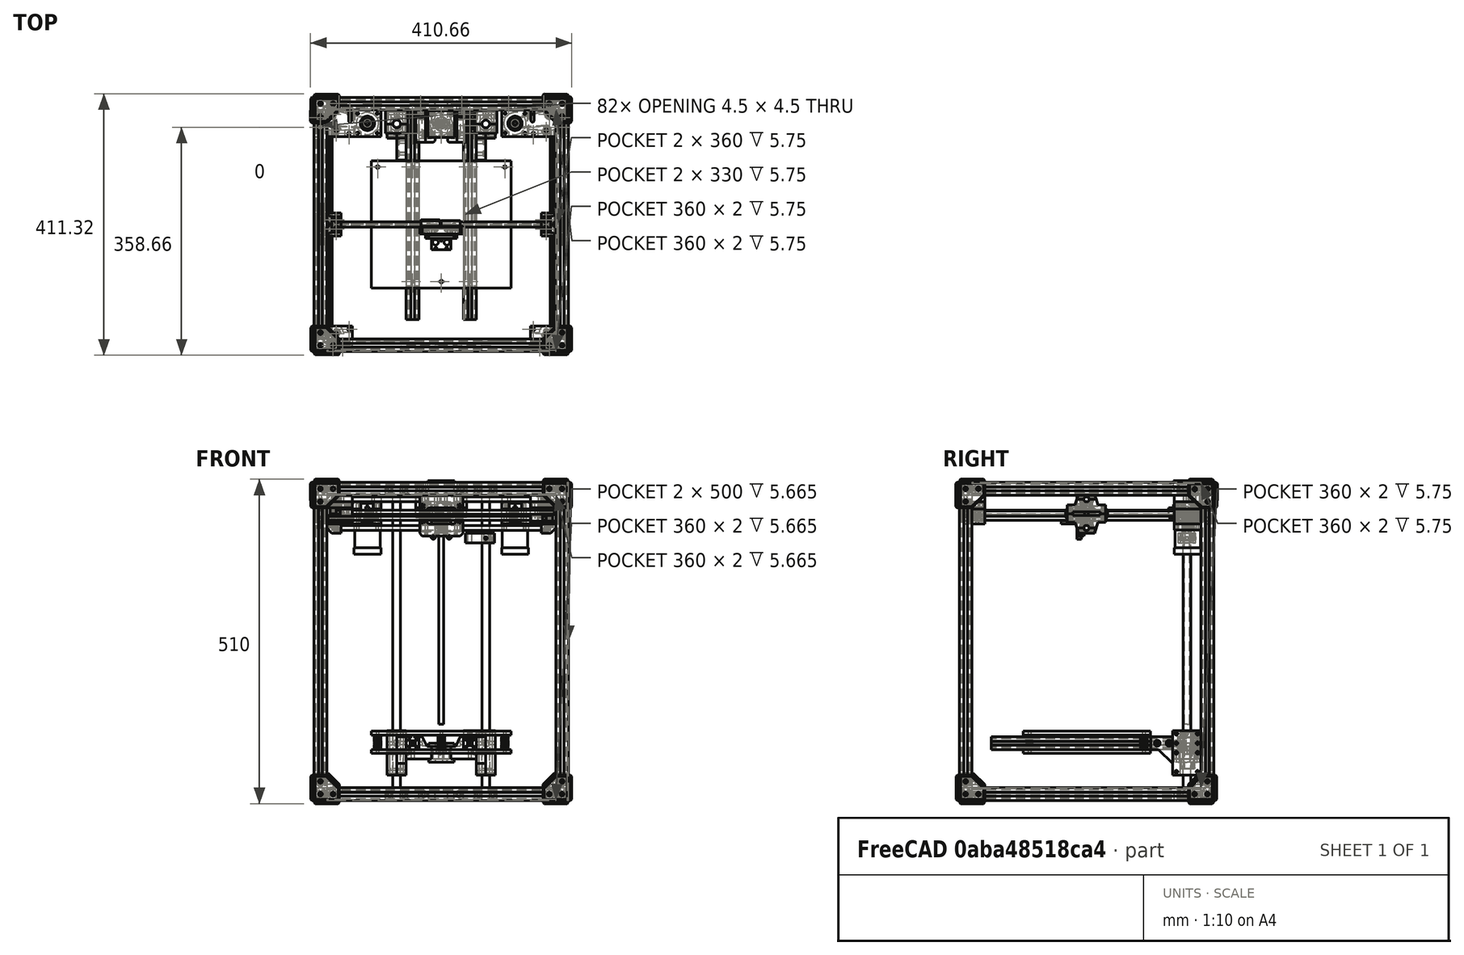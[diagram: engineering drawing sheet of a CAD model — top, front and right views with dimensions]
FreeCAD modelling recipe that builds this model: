
FCSTD DOCUMENT  (FreeCAD 0.16R5937 (Git))
Label: RepRap-XY-Iteration-2-Assembly
License: CC-BY 3.0
LicenseURL: http://creativecommons.org/licenses/by/3.0/
objects: Part::Feature×185, Part::Prism×30, Part::Fuse×25, Part::Box×15, Part::FeaturePython×6, Part::Cylinder×6, Part::Cut×6, Part::Extrusion×3, Part::MultiFuse×3, Part::Mirroring×1
note: 280 computed .brp shape members not serialized (recipe doc carries the construction recipe); baked Part::Feature solids carry a one-line shape summary decoded from their .brp

FEATURE [Part::Feature] Part__Feature  label="Nema-17"
  shape: bbox 42 x 42 x 74.5 mm, 37 faces (baked)
FEATURE [Part::Feature] Part__Feature001  label="Nema-018"
  shape: bbox 42 x 42 x 74.5 mm, 37 faces (baked)
FEATURE [Part::Feature] Part__Feature002  label="Nema-019"
  Placement = pos=(0,0,10) rot=(0,0,1;0rad)
  shape: bbox 42 x 42 x 74.5 mm, 37 faces (baked)
FEATURE [Part::Feature] Part__Feature004  label="F624zz-bearing"
  shape: bbox 15 x 15 x 5 mm, 15 faces (baked)
FEATURE [Part::Feature] Part__Feature005  label="624-bearing"
  shape: bbox 13 x 13 x 5 mm, 10 faces (baked)
FEATURE [Part::Feature] Part__Feature006  label="spacer-1"
  shape: bbox 10 x 10 x 9.4 mm, 6 faces (baked)
FEATURE [Part::Feature] Part__Feature007  label="F624zz-bearing001"
  shape: bbox 15 x 15 x 5 mm, 15 faces (baked)
FEATURE [Part::Feature] Part__Feature008  label="624-bearing001"
  shape: bbox 13 x 13 x 5 mm, 10 faces (baked)
FEATURE [Part::Feature] Part__Feature009  label="washer-M4"
  shape: bbox 8 x 8 x 0.8 mm, 6 faces (baked)
FEATURE [Part::Feature] Part__Feature010  label="washer-M005"
  shape: bbox 8 x 8 x 0.8 mm, 6 faces (baked)
FEATURE [Part::Feature] Part__Feature011  label="F624zz-bearing002"
  shape: bbox 15 x 15 x 5 mm, 15 faces (baked)
FEATURE [Part::Feature] Part__Feature012  label="624-bearing002"
  shape: bbox 13 x 13 x 5 mm, 10 faces (baked)
FEATURE [Part::Feature] Part__Feature013  label="washer-M006"
  shape: bbox 8 x 8 x 0.8 mm, 6 faces (baked)
FEATURE [Part::Feature] Part__Feature014  label="washer-M007"
  shape: bbox 8 x 8 x 0.8 mm, 6 faces (baked)
FEATURE [Part::Feature] Part__Feature015  label="F624zz-bearing003"
  shape: bbox 15 x 15 x 5 mm, 15 faces (baked)
FEATURE [Part::Feature] Part__Feature016  label="624-bearing003"
  shape: bbox 13 x 13 x 5 mm, 10 faces (baked)
FEATURE [Part::Feature] Part__Feature017  label="washer-M008"
  shape: bbox 8 x 8 x 0.8 mm, 6 faces (baked)
FEATURE [Part::Feature] Part__Feature018  label="washer-M009"
  shape: bbox 8 x 8 x 0.8 mm, 6 faces (baked)
FEATURE [Part::Feature] Part__Feature019  label="F624zz-bearing004"
  shape: bbox 15 x 15 x 5 mm, 15 faces (baked)
FEATURE [Part::Feature] Part__Feature020  label="624-bearing004"
  shape: bbox 13 x 13 x 5 mm, 10 faces (baked)
FEATURE [Part::Feature] Part__Feature021  label="washer-M010"
  shape: bbox 8 x 8 x 0.8 mm, 6 faces (baked)
FEATURE [Part::Feature] Part__Feature022  label="washer-M011"
  shape: bbox 8 x 8 x 0.8 mm, 6 faces (baked)
FEATURE [Part::Feature] Part__Feature023  label="washer-M012"
  shape: bbox 8 x 8 x 0.8 mm, 6 faces (baked)
FEATURE [Part::Feature] Part__Feature024  label="washer-M013"
  shape: bbox 8 x 8 x 0.8 mm, 6 faces (baked)
FEATURE [Part::Feature] Part__Feature025  label="F624zz-bearing005"
  shape: bbox 15 x 15 x 5 mm, 15 faces (baked)
FEATURE [Part::Feature] Part__Feature026  label="624-bearing005"
  shape: bbox 13 x 13 x 5 mm, 10 faces (baked)
FEATURE [Part::Feature] Part__Feature027  label="spacer-002"
  shape: bbox 10 x 10 x 9.4 mm, 6 faces (baked)
FEATURE [Part::Feature] Part__Feature028  label="washer-M014"
  shape: bbox 8 x 8 x 0.8 mm, 6 faces (baked)
FEATURE [Part::Feature] Part__Feature029  label="washer-M015"
  shape: bbox 8 x 8 x 0.8 mm, 6 faces (baked)
FEATURE [Part::Feature] Part__Feature030  label="F624zz-bearing006"
  shape: bbox 15 x 15 x 5 mm, 15 faces (baked)
FEATURE [Part::Feature] Part__Feature031  label="624-bearing006"
  shape: bbox 13 x 13 x 5 mm, 10 faces (baked)
FEATURE [Part::Feature] Part__Feature032  label="spacer-003"
  shape: bbox 10 x 10 x 9.4 mm, 6 faces (baked)
FEATURE [Part::Feature] Part__Feature033  label="washer-M016"
  shape: bbox 8 x 8 x 0.8 mm, 6 faces (baked)
FEATURE [Part::Feature] Part__Feature034  label="washer-M017"
  shape: bbox 8 x 8 x 0.8 mm, 6 faces (baked)
FEATURE [Part::Feature] Part__Feature035  label="F624zz-bearing007"
  shape: bbox 15 x 15 x 5 mm, 15 faces (baked)
FEATURE [Part::Feature] Part__Feature036  label="624-bearing007"
  shape: bbox 13 x 13 x 5 mm, 10 faces (baked)
FEATURE [Part::Feature] Part__Feature037  label="spacer-004"
  shape: bbox 10 x 10 x 9.4 mm, 6 faces (baked)
FEATURE [Part::Feature] Part__Feature038  label="washer-M018"
  shape: bbox 8 x 8 x 0.8 mm, 6 faces (baked)
FEATURE [Part::Feature] Part__Feature039  label="washer-M019"
  shape: bbox 8 x 8 x 0.8 mm, 6 faces (baked)
FEATURE [Part::Feature] Part__Feature040  label="F624zz-bearing008"
  shape: bbox 15 x 15 x 5 mm, 15 faces (baked)
FEATURE [Part::Feature] Part__Feature041  label="624-bearing008"
  shape: bbox 13 x 13 x 5 mm, 10 faces (baked)
FEATURE [Part::Feature] Part__Feature042  label="washer-M020"
  shape: bbox 8 x 8 x 0.8 mm, 6 faces (baked)
FEATURE [Part::Feature] Part__Feature043  label="washer-M021"
  shape: bbox 8 x 8 x 0.8 mm, 6 faces (baked)
FEATURE [Part::Feature] Part__Feature044  label="F624zz-bearing009"
  shape: bbox 15 x 15 x 5 mm, 15 faces (baked)
FEATURE [Part::Feature] Part__Feature045  label="624-bearing009"
  shape: bbox 13 x 13 x 5 mm, 10 faces (baked)
FEATURE [Part::Feature] Part__Feature046  label="washer-M022"
  shape: bbox 8 x 8 x 0.8 mm, 6 faces (baked)
FEATURE [Part::Feature] Part__Feature047  label="washer-M023"
  shape: bbox 8 x 8 x 0.8 mm, 6 faces (baked)
FEATURE [Part::Feature] Part__Feature048  label="F624zz-bearing010"
  shape: bbox 15 x 15 x 5 mm, 15 faces (baked)
FEATURE [Part::Feature] Part__Feature049  label="624-bearing010"
  shape: bbox 13 x 13 x 5 mm, 10 faces (baked)
FEATURE [Part::Feature] Part__Feature050  label="washer-M024"
  shape: bbox 8 x 8 x 0.8 mm, 6 faces (baked)
FEATURE [Part::Feature] Part__Feature051  label="washer-M025"
  shape: bbox 8 x 8 x 0.8 mm, 6 faces (baked)
FEATURE [Part::Feature] Part__Feature052  label="F624zz-bearing011"
  shape: bbox 15 x 15 x 5 mm, 15 faces (baked)
FEATURE [Part::Feature] Part__Feature053  label="624-bearing011"
  shape: bbox 13 x 13 x 5 mm, 10 faces (baked)
FEATURE [Part::Feature] Part__Feature054  label="washer-M026"
  shape: bbox 8 x 8 x 0.8 mm, 6 faces (baked)
FEATURE [Part::Feature] Part__Feature055  label="washer-M027"
  shape: bbox 8 x 8 x 0.8 mm, 6 faces (baked)
FEATURE [Part::Feature] Part__Feature057  label="Alu-20x20x360"
  Placement = pos=(0,0,-110) rot=(0,0,1;0rad)
  shape: bbox 360 x 20 x 20 mm, 40 faces (baked)
FEATURE [Part::Feature] Part__Feature058  label="Alu-20x20x361"
  Placement = pos=(0,0,-110) rot=(0,0,1;0rad)
  shape: bbox 20 x 360 x 20 mm, 40 faces (baked)
FEATURE [Part::Feature] Part__Feature059  label="Alu-20x20x362"
  Placement = pos=(0,0,-110) rot=(0,0,1;0rad)
  shape: bbox 20 x 360 x 20 mm, 40 faces (baked)
FEATURE [Part::Feature] Part__Feature060  label="Alu-20x20x363"
  Placement = pos=(0,0,-110) rot=(0,0,1;0rad)
  shape: bbox 360 x 20 x 20 mm, 40 faces (baked)
FEATURE [Part::Feature] Part__Feature064  label="Alu-20x20x367"
  Placement = pos=(0,0,10) rot=(0,0,1;0rad)
  shape: bbox 360 x 20 x 20 mm, 40 faces (baked)
FEATURE [Part::Feature] Part__Feature065  label="Alu-20x20x368"
  Placement = pos=(0,0,10) rot=(0,0,1;0rad)
  shape: bbox 20 x 360 x 20 mm, 40 faces (baked)
FEATURE [Part::Feature] Part__Feature066  label="Alu-20x20x369"
  Placement = pos=(0,0,10) rot=(0,0,1;0rad)
  shape: bbox 20 x 360 x 20 mm, 40 faces (baked)
FEATURE [Part::Feature] Part__Feature067  label="Alu-20x20x370"
  Placement = pos=(0,0,10) rot=(0,0,1;0rad)
  shape: bbox 360 x 20 x 20 mm, 40 faces (baked)
FEATURE [Part::Feature] Part__Feature068  label="smooth-bar-8x330"
  Placement = pos=(0,20,22.5) rot=(0,0,1;0rad)
  shape: bbox 330 x 8 x 8 mm, 4 faces (baked)
FEATURE [Part::Feature] Part__Feature069  label="smooth-bar-8x331"
  shape: bbox 8 x 330 x 8 mm, 4 faces (baked)
FEATURE [Part::Feature] Part__Feature070  label="smooth-bar-8x332"
  shape: bbox 8 x 330 x 8 mm, 4 faces (baked)
FEATURE [Part::Feature] Part__Feature071  label="smooth-bar-8x333"
  Placement = pos=(0,-20,-22.5) rot=(0,0,1;0rad)
  shape: bbox 330 x 8 x 8 mm, 4 faces (baked)
FEATURE [Part::Feature] Part__Feature072  label="Alu-20x20x330"
  Placement = pos=(0,0,-280) rot=(0,0,1;0rad)
  shape: bbox 20 x 330 x 20 mm, 40 faces (baked)
FEATURE [Part::Feature] Part__Feature073  label="Alu-20x20x371"
  Placement = pos=(0,0,-280) rot=(0,0,1;0rad)
  shape: bbox 20 x 330 x 20 mm, 41 faces (baked)
FEATURE [Part::Feature] Part__Feature077  label="GT2-belt"
  shape: bbox 351 x 379 x 6 mm, 36 faces (baked)
FEATURE [Part::Feature] Part__Feature078  label="GT2-belt001"
  shape: bbox 351 x 379 x 6 mm, 36 faces (baked)
FEATURE [Part::Feature] Part__Feature083  label="idler-block"
  shape: bbox 60 x 40 x 23 mm, 30 faces (baked)
FEATURE [Part::Feature] Part__Feature084  label="idler-block-top"
  shape: bbox 60 x 40 x 12 mm, 28 faces (baked)
FEATURE [Part::Feature] Part__Feature085  label="idler-block-mirrored"
  shape: bbox 60 x 40 x 23 mm, 30 faces (baked)
FEATURE [Part::Feature] Part__Feature086  label="idler-block-top-mirrored"
  shape: bbox 60 x 40 x 12 mm, 28 faces (baked)
FEATURE [Part::Feature] Part__Feature088  label="624-bearing012"
  shape: bbox 13 x 13 x 5 mm, 10 faces (baked)
FEATURE [Part::Feature] Part__Feature089  label="624-bearing013"
  shape: bbox 13 x 13 x 5 mm, 10 faces (baked)
FEATURE [Part::Feature] Part__Feature090  label="Z-axis-clamp-1"
  Placement = pos=(0,0,-110) rot=(0,0,1;0rad)
  shape: bbox 35 x 22 x 20 mm, 12 faces (baked)
FEATURE [Part::Feature] Part__Feature091  label="Z-axis-clamp-002"
  Placement = pos=(0,0,-110) rot=(0,0,1;0rad)
  shape: bbox 35 x 22 x 20 mm, 12 faces (baked)
FEATURE [Part::Feature] Part__Feature092  label="Z-axis-clamp-003"
  Placement = pos=(0,0,10) rot=(0,0,1;0rad)
  shape: bbox 35 x 22 x 20 mm, 12 faces (baked)
FEATURE [Part::Feature] Part__Feature093  label="Z-axis-clamp-004"
  Placement = pos=(0,0,10) rot=(0,0,1;0rad)
  shape: bbox 35 x 22 x 20 mm, 12 faces (baked)
FEATURE [Part::Feature] Part__Feature094  label="spacer-7mm"
  shape: bbox 10 x 10 x 7 mm, 6 faces (baked)
FEATURE [Part::Feature] Part__Feature095  label="spacer-7mm001"
  shape: bbox 10 x 10 x 7 mm, 6 faces (baked)
FEATURE [Part::Feature] Part__Feature096  label="spacer-9mm4"
  shape: bbox 10 x 10 x 9.4 mm, 6 faces (baked)
FEATURE [Part::Feature] Part__Feature097  label="spacer-9mm005"
  shape: bbox 10 x 10 x 9.4 mm, 6 faces (baked)
FEATURE [Part::Feature] Part__Feature098  label="spacer-9mm006"
  shape: bbox 10 x 10 x 9.4 mm, 6 faces (baked)
FEATURE [Part::Feature] Part__Feature099  label="spacer-9mm007"
  shape: bbox 10 x 10 x 9.4 mm, 6 faces (baked)
FEATURE [Part::Feature] Part__Feature100  label="spacer-9mm008"
  shape: bbox 10 x 10 x 9.4 mm, 6 faces (baked)
FEATURE [Part::Feature] Part__Feature101  label="spacer-9mm009"
  shape: bbox 10 x 10 x 9.4 mm, 6 faces (baked)
FEATURE [Part::Feature] Part__Feature102  label="spacer16mm4"
  shape: bbox 10 x 10 x 16.4 mm, 6 faces (baked)
FEATURE [Part::Feature] Part__Feature103  label="spacer16mm005"
  shape: bbox 10 x 10 x 16.4 mm, 6 faces (baked)
FEATURE [Part::Feature] Part__Feature104  label="spacer16mm006"
  shape: bbox 10 x 10 x 16.4 mm, 6 faces (baked)
FEATURE [Part::Feature] Part__Feature105  label="washer-M028"
  shape: bbox 8 x 8 x 0.8 mm, 6 faces (baked)
FEATURE [Part::Feature] Part__Feature106  label="Z-axis-clamp-2"
  Placement = pos=(0,0,10) rot=(0,0,1;0rad)
  shape: bbox 35 x 15 x 20 mm, 18 faces (baked)
FEATURE [Part::Feature] Part__Feature107  label="Z-axis-clamp-005"
  Placement = pos=(0,0,10) rot=(0,0,1;0rad)
  shape: bbox 35 x 15 x 20 mm, 18 faces (baked)
FEATURE [Part::Feature] Part__Feature108  label="Z-axis-clamp-006"
  Placement = pos=(0,0,-110) rot=(0,0,1;0rad)
  shape: bbox 35 x 15 x 20 mm, 18 faces (baked)
FEATURE [Part::Feature] Part__Feature109  label="Z-axis-clamp-007"
  Placement = pos=(0,0,-110) rot=(0,0,1;0rad)
  shape: bbox 35 x 15 x 20 mm, 18 faces (baked)
FEATURE [Part::Feature] Part__Feature122  label="pulley"
  shape: bbox 17.78 x 17.78 x 16.13 mm, 138 faces (baked)
FEATURE [Part::Feature] Part__Feature123  label="pulley001"
  shape: bbox 17.78 x 17.78 x 16.13 mm, 138 faces (baked)
FEATURE [Part::Feature] Part__Feature130  label="Z-motor-mount"
  Placement = pos=(0,0,10) rot=(0,0,1;0rad)
  shape: bbox 30.05 x 100 x 85.05 mm, 39 faces (baked)
FEATURE [Part::Feature] Part__Feature131  label="Z-motor-mount-mirrored"
  Placement = pos=(0,0,10) rot=(0,0,1;0rad)
  shape: bbox 30.05 x 100 x 85.05 mm, 39 faces (baked)
FEATURE [Part::Feature] Part__Feature132  label="Z-block-1"
  Placement = pos=(0,0,-280) rot=(0,0,1;0rad)
  shape: bbox 15 x 79.2 x 70 mm, 45 faces (baked)
FEATURE [Part::Feature] Part__Feature133  label="Z-block-1-mirrored"
  Placement = pos=(0,0,-280) rot=(0,0,1;0rad)
  shape: bbox 15 x 79.2 x 70 mm, 45 faces (baked)
FEATURE [Part::Feature] Part__Feature134  label="Z-block-2"
  Placement = pos=(0,0,-280) rot=(0,0,1;0rad)
  shape: bbox 15 x 45 x 70 mm, 30 faces (baked)
FEATURE [Part::Feature] Part__Feature135  label="Z-block-003"
  Placement = pos=(0,0,-280) rot=(0,0,1;0rad)
  shape: bbox 15 x 45 x 70 mm, 30 faces (baked)
FEATURE [Part::Feature] Part__Feature136  label="bed"
  Placement = pos=(0,0,-280) rot=(0,0,1;0rad)
  shape: bbox 220 x 200 x 6 mm, 20 faces (baked)
FEATURE [Part::Feature] Part__Feature137  label="heat-spreader"
  Placement = pos=(0,0,-280) rot=(0,0,1;0rad)
  shape: bbox 220 x 200 x 6 mm, 12 faces (baked)
FEATURE [Part::Feature] Part__Feature138  label="spring"
  Placement = pos=(0,0,-280) rot=(0,0,1;0rad)
  shape: bbox 12.42 x 12.43 x 24.52 mm, 4 faces (baked)
FEATURE [Part::Feature] Part__Feature139  label="spring001"
  Placement = pos=(0,0,-280) rot=(0,0,1;0rad)
  shape: bbox 12.42 x 12.43 x 24.52 mm, 4 faces (baked)
FEATURE [Part::Feature] Part__Feature140  label="spring002"
  Placement = pos=(0,0,-280) rot=(0,0,1;0rad)
  shape: bbox 12.42 x 12.43 x 24.52 mm, 4 faces (baked)
FEATURE [Part::Feature] Part__Feature141  label="nut-M8"
  Placement = pos=(0,0,-280) rot=(0,0,1;0rad)
  shape: bbox 15.01 x 13 x 6.2 mm, 10 faces (baked)
FEATURE [Part::Feature] Part__Feature142  label="nut-M009"
  Placement = pos=(0,0,-280) rot=(0,0,1;0rad)
  shape: bbox 15.01 x 13 x 6.2 mm, 10 faces (baked)
FEATURE [Part::Feature] Part__Feature143  label="Z-nut-1"
  Placement = pos=(0,0,-280) rot=(0,0,1;0rad)
  shape: bbox 25 x 13 x 20 mm, 14 faces (baked)
FEATURE [Part::Feature] Part__Feature144  label="Z-nut-2"
  Placement = pos=(0,0,-280) rot=(0,0,1;0rad)
  shape: bbox 40 x 40 x 25 mm, 30 faces (baked)
FEATURE [Part::Feature] Part__Feature145  label="Z-nut-4"
  Placement = pos=(0,0,-280) rot=(0,0,1;0rad)
  shape: bbox 40 x 40 x 5 mm, 16 faces (baked)
FEATURE [Part::Feature] Part__Feature146  label="Z-nut-3"
  Placement = pos=(0,0,-280) rot=(0,0,1;0rad)
  shape: bbox 40 x 45 x 35 mm, 44 faces (baked)
FEATURE [Part::Feature] Part__Feature147  label="Z-nut-005"
  Placement = pos=(0,0,-280) rot=(0,0,1;0rad)
  shape: bbox 40 x 45 x 35 mm, 44 faces (baked)
FEATURE [Part::Feature] Part__Feature148  label="Z-endstop-mount"
  shape: bbox 46.15 x 27.9 x 15 mm, 39 faces (baked)
FEATURE [Part::Feature] Part__Feature150  label="Z-endstop-adjust"
  Placement = pos=(0,0,-280) rot=(0,0,1;0rad)
  shape: bbox 20 x 20 x 12 mm, 27 faces (baked)
FEATURE [Part::Feature] Part__Feature151  label="lead-screw"
  Placement = pos=(0,0,10) rot=(0,0,1;0rad)
  shape: bbox 8 x 8 x 307 mm, 4 faces (baked)
FEATURE [Part::Feature] Part__Feature152  label="608-bearing"
  Placement = pos=(0,0,-110) rot=(0,0,1;0rad)
  shape: bbox 22 x 22 x 6.9 mm, 11 faces (baked)
FEATURE [Part::Feature] Part__Feature153  label="Z-leadscrew-bearing-block"
  Placement = pos=(0,0,-110) rot=(0,0,1;0rad)
  shape: bbox 70 x 42 x 20 mm, 25 faces (baked)
FEATURE [Part::Feature] Part__Feature156  label="motor-block"
  shape: bbox 105 x 62 x 23 mm, 59 faces (baked)
FEATURE [Part::Feature] Part__Feature157  label="motor-block-top"
  shape: bbox 105 x 62 x 12 mm, 56 faces (baked)
FEATURE [Part::Feature] Part__Feature158  label="motor-block-mirrored"
  shape: bbox 105 x 62 x 23 mm, 59 faces (baked)
FEATURE [Part::Box] cube
  Height = 13.5
  Length = 60.2
  Width = 20
FEATURE [Part::Box] cube001
  Height = 1
  Length = 24.98
  Placement = pos=(17.61,0,29.5) rot=(0,0,1;0rad)
  Width = 42.5
FEATURE [Part::Box] cube002
  Height = 13.5
  Length = 36
  Placement = pos=(12.1,0,0) rot=(0,0,1;0rad)
  Width = 42.5
FEATURE [Part::FeaturePython] hull  # WARN: FeaturePython — macro-defined, semantics opaque (R4)
  Arguments = []
  Children = -> [cube001,cube002]
  Operation = hull
FEATURE [Part::Fuse] union
  Base = -> cube
  Tool = -> hull
FEATURE [Part::Prism] prism
  Circumradius = 7.6
  Height = 60.4
  Placement = pos=(-0.1,10,0) rot=(0,1,0;1.5708rad)
  Polygon = 30
FEATURE [Part::Box] cube003
  Height = 3
  Length = 43
  Placement = pos=(8.6,0,0) rot=(0,0,1;0rad)
  Width = 20
FEATURE [Part::Prism] prism001
  Circumradius = 4.1
  Height = 42.7
  Placement = pos=(30.1,42.6,22.5) rot=(1,0,0;1.5708rad)
  Polygon = 30
FEATURE [Part::Box] cube004
  Height = 11.6
  Length = 36.2
  Placement = pos=(12,20,0) rot=(0,0,1;0rad)
  Width = 42.5
FEATURE [Part::Cylinder] cylinder
  Angle = 360
  Height = 61
  Radius = 2.3
FEATURE [Part::Prism] prism002
  Circumradius = 4.5
  Height = 4
  Placement = pos=(0,0,26.5) rot=(0,0,1;0rad)
  Polygon = 60
FEATURE [Part::Fuse] Matrix_Union
  Base = -> cylinder
  Placement = pos=(22.91,36,0) rot=(0,0,1;0rad)
  Tool = -> prism002
FEATURE [Part::Cylinder] cylinder001
  Angle = 360
  Height = 61
  Radius = 2.3
FEATURE [Part::Prism] prism003
  Circumradius = 4.5
  Height = 4
  Placement = pos=(0,0,26.5) rot=(0,0,1;0rad)
  Polygon = 60
FEATURE [Part::Fuse] Matrix_Union001
  Base = -> cylinder001
  Placement = pos=(37.29,36,0) rot=(0,0,1;0rad)
  Tool = -> prism003
FEATURE [Part::Fuse] Group
  Base = -> Matrix_Union
  Tool = -> Matrix_Union001
FEATURE [Part::Prism] prism004
  Circumradius = 1.8
  Height = 61
  Placement = pos=(-25.8,6,0) rot=(0,0,1;0rad)
  Polygon = 60
FEATURE [Part::Prism] prism005
  Circumradius = 1.8
  Height = 61
  Placement = pos=(-25.8,-6,0) rot=(0,0,1;0rad)
  Polygon = 60
FEATURE [Part::Fuse] Group001
  Base = -> prism004
  Tool = -> prism005
FEATURE [Part::Prism] prism006
  Circumradius = 1.8
  Height = 61
  Placement = pos=(25.8,6,0) rot=(0,0,1;0rad)
  Polygon = 60
FEATURE [Part::Prism] prism007
  Circumradius = 1.8
  Height = 61
  Placement = pos=(25.8,-6,0) rot=(0,0,1;0rad)
  Polygon = 60
FEATURE [Part::Fuse] Group002
  Base = -> prism006
  Tool = -> prism007
FEATURE [Part::Fuse] Group003
  Base = -> Group001
  Placement = pos=(30.1,10,0) rot=(0,0,1;0rad)
  Tool = -> Group002
FEATURE [Part::Feature] polygon
  shape: bbox 28 x 8 x 2e-07 mm, 1 faces, 0 solids (baked)
FEATURE [Part::FeaturePython] RefineLinearExtrude  # WARN: FeaturePython — macro-defined, semantics opaque (R4)
  Base = -> polygon
FEATURE [Part::Extrusion] LinearExtrude
  Base = -> RefineLinearExtrude
  Dir = (0,0,42.5)
  Placement = pos=(51.35,20,22.5) rot=(-0.57735,0.57735,0.57735;4.18879rad)
  Solid = true
FEATURE [Part::Prism] prism008
  Circumradius = 11
  Height = 6
  Placement = pos=(0,3,0) rot=(1,0,0;1.5708rad)
  Polygon = 30
FEATURE [Part::Prism] prism009
  Circumradius = 8
  Height = 6
  Placement = pos=(0,3,0) rot=(1,0,0;1.5708rad)
  Polygon = 40
FEATURE [Part::Cut] difference
  Base = -> prism008
  Placement = pos=(30.1,10,22.5) rot=(0,0,1;0rad)
  Tool = -> prism009
FEATURE [Part::Fuse] Group004
  Base = -> LinearExtrude
  Tool = -> difference
FEATURE [Part::MultiFuse] union001
  Shapes = -> [prism,cube003,prism001,cube004,Group,Group003,Group004]
FEATURE [Part::Cut] difference001
  Base = -> union
  Tool = -> union001
FEATURE [Part::Box] cube005
  Height = 13.5
  Length = 60.2
  Width = 20
FEATURE [Part::Box] cube006
  Height = 1
  Length = 24.98
  Placement = pos=(17.61,0,29.5) rot=(0,0,1;0rad)
  Width = 42.5
FEATURE [Part::Box] cube007
  Height = 13.5
  Length = 36
  Placement = pos=(12.1,0,0) rot=(0,0,1;0rad)
  Width = 42.5
FEATURE [Part::FeaturePython] hull001  # WARN: FeaturePython — macro-defined, semantics opaque (R4)
  Arguments = []
  Children = -> [cube006,cube007]
  Operation = hull
FEATURE [Part::Fuse] union002
  Base = -> cube005
  Tool = -> hull001
FEATURE [Part::Prism] prism010
  Circumradius = 7.6
  Height = 60.4
  Placement = pos=(-0.1,10,0) rot=(0,1,0;1.5708rad)
  Polygon = 30
FEATURE [Part::Box] cube008
  Height = 3
  Length = 43
  Placement = pos=(8.6,0,0) rot=(0,0,1;0rad)
  Width = 20
FEATURE [Part::Prism] prism011
  Circumradius = 4.1
  Height = 42.7
  Placement = pos=(30.1,42.6,22.5) rot=(1,0,0;1.5708rad)
  Polygon = 30
FEATURE [Part::Box] cube009
  Height = 11.6
  Length = 36.2
  Placement = pos=(12,20,0) rot=(0,0,1;0rad)
  Width = 42.5
FEATURE [Part::Cylinder] cylinder002
  Angle = 360
  Height = 61
  Radius = 2.3
FEATURE [Part::Prism] prism012
  Circumradius = 4.075
  Height = 4
  Placement = pos=(0,0,26.5) rot=(0,0,1;0rad)
  Polygon = 6
FEATURE [Part::Fuse] Matrix_Union002
  Base = -> cylinder002
  Placement = pos=(22.91,36,0) rot=(0,0,1;0rad)
  Tool = -> prism012
FEATURE [Part::Cylinder] cylinder003
  Angle = 360
  Height = 61
  Radius = 2.3
FEATURE [Part::Prism] prism013
  Circumradius = 4.075
  Height = 4
  Placement = pos=(0,0,26.5) rot=(0,0,1;0rad)
  Polygon = 6
FEATURE [Part::Fuse] Matrix_Union003
  Base = -> cylinder003
  Placement = pos=(37.29,36,0) rot=(0,0,1;0rad)
  Tool = -> prism013
FEATURE [Part::Fuse] Group005
  Base = -> Matrix_Union002
  Tool = -> Matrix_Union003
FEATURE [Part::Prism] prism014
  Circumradius = 1.8
  Height = 61
  Placement = pos=(-25.8,6,0) rot=(0,0,1;0rad)
  Polygon = 60
FEATURE [Part::Prism] prism015
  Circumradius = 1.8
  Height = 61
  Placement = pos=(-25.8,-6,0) rot=(0,0,1;0rad)
  Polygon = 60
FEATURE [Part::Fuse] Group006
  Base = -> prism014
  Tool = -> prism015
FEATURE [Part::Prism] prism016
  Circumradius = 1.8
  Height = 61
  Placement = pos=(25.8,6,0) rot=(0,0,1;0rad)
  Polygon = 60
FEATURE [Part::Prism] prism017
  Circumradius = 1.8
  Height = 61
  Placement = pos=(25.8,-6,0) rot=(0,0,1;0rad)
  Polygon = 60
FEATURE [Part::Fuse] Group007
  Base = -> prism016
  Tool = -> prism017
FEATURE [Part::Fuse] Group008
  Base = -> Group006
  Placement = pos=(30.1,10,0) rot=(0,0,1;0rad)
  Tool = -> Group007
FEATURE [Part::Feature] polygon001
  shape: bbox 28 x 8 x 2e-07 mm, 1 faces, 0 solids (baked)
FEATURE [Part::FeaturePython] RefineLinearExtrude001  # WARN: FeaturePython — macro-defined, semantics opaque (R4)
  Base = -> polygon001
FEATURE [Part::Extrusion] LinearExtrude001
  Base = -> RefineLinearExtrude001
  Dir = (0,0,42.5)
  Placement = pos=(51.35,20,22.5) rot=(-0.57735,0.57735,0.57735;4.18879rad)
  Solid = true
FEATURE [Part::Prism] prism018
  Circumradius = 11
  Height = 6
  Placement = pos=(0,3,0) rot=(1,0,0;1.5708rad)
  Polygon = 30
FEATURE [Part::Prism] prism019
  Circumradius = 8
  Height = 6
  Placement = pos=(0,3,0) rot=(1,0,0;1.5708rad)
  Polygon = 40
FEATURE [Part::Cut] difference002
  Base = -> prism018
  Placement = pos=(30.1,10,22.5) rot=(0,0,1;0rad)
  Tool = -> prism019
FEATURE [Part::Fuse] Group009
  Base = -> LinearExtrude001
  Tool = -> difference002
FEATURE [Part::MultiFuse] union003
  Shapes = -> [prism010,cube008,prism011,cube009,Group005,Group008,Group009]
FEATURE [Part::Cut] difference003
  Base = -> union002
  Tool = -> union003
FEATURE [Part::Mirroring] mirr_difference003  label="mirrored difference003"
  Base = (0,0,0)
  Normal = (0,0,1)
  Placement = pos=(0,0,-5) rot=(0,0,1;0rad)
  Source = -> difference003
FEATURE [Part::Fuse] Group010
  Base = -> difference001
  Tool = -> mirr_difference003
FEATURE [Part::Box] cube010
  Height = 13.5
  Length = 60.2
  Width = 20
FEATURE [Part::Box] cube011
  Height = 1
  Length = 24.98
  Placement = pos=(17.61,0,29.5) rot=(0,0,1;0rad)
  Width = 42.5
FEATURE [Part::Box] cube012
  Height = 13.5
  Length = 36
  Placement = pos=(12.1,0,0) rot=(0,0,1;0rad)
  Width = 42.5
FEATURE [Part::FeaturePython] hull002  # WARN: FeaturePython — macro-defined, semantics opaque (R4)
  Arguments = []
  Children = -> [cube011,cube012]
  Operation = hull
FEATURE [Part::Fuse] union004
  Base = -> cube010
  Tool = -> hull002
FEATURE [Part::Prism] prism020
  Circumradius = 6.1
  Height = 60.4
  Placement = pos=(-0.1,10,0) rot=(0,1,0;1.5708rad)
  Polygon = 30
FEATURE [Part::Box] cube013
  Height = 3
  Length = 43
  Placement = pos=(8.6,0,0) rot=(0,0,1;0rad)
  Width = 20
FEATURE [Part::Prism] prism021
  Circumradius = 4.1
  Height = 42.7
  Placement = pos=(30.1,42.6,22.5) rot=(1,0,0;1.5708rad)
  Polygon = 30
FEATURE [Part::Box] cube014
  Height = 11.6
  Length = 36.2
  Placement = pos=(12,20,0) rot=(0,0,1;0rad)
  Width = 42.5
FEATURE [Part::Cylinder] cylinder004
  Angle = 360
  Height = 61
  Radius = 2.3
FEATURE [Part::Prism] prism022
  Circumradius = 4.5
  Height = 4
  Placement = pos=(0,0,26.5) rot=(0,0,1;0rad)
  Polygon = 60
FEATURE [Part::Fuse] Matrix_Union004
  Base = -> cylinder004
  Placement = pos=(22.91,36,0) rot=(0,0,1;0rad)
  Tool = -> prism022
FEATURE [Part::Cylinder] cylinder005
  Angle = 360
  Height = 61
  Radius = 2.3
FEATURE [Part::Prism] prism023
  Circumradius = 4.5
  Height = 4
  Placement = pos=(0,0,26.5) rot=(0,0,1;0rad)
  Polygon = 60
FEATURE [Part::Fuse] Matrix_Union005
  Base = -> cylinder005
  Placement = pos=(37.29,36,0) rot=(0,0,1;0rad)
  Tool = -> prism023
FEATURE [Part::Fuse] Group011
  Base = -> Matrix_Union004
  Tool = -> Matrix_Union005
FEATURE [Part::Prism] prism024
  Circumradius = 1.8
  Height = 61
  Placement = pos=(-25.8,6,0) rot=(0,0,1;0rad)
  Polygon = 60
FEATURE [Part::Prism] prism025
  Circumradius = 1.8
  Height = 61
  Placement = pos=(-25.8,-6,0) rot=(0,0,1;0rad)
  Polygon = 60
FEATURE [Part::Fuse] Group012
  Base = -> prism024
  Tool = -> prism025
FEATURE [Part::Prism] prism026
  Circumradius = 1.8
  Height = 61
  Placement = pos=(25.8,6,0) rot=(0,0,1;0rad)
  Polygon = 60
FEATURE [Part::Prism] prism027
  Circumradius = 1.8
  Height = 61
  Placement = pos=(25.8,-6,0) rot=(0,0,1;0rad)
  Polygon = 60
FEATURE [Part::Fuse] Group013
  Base = -> prism026
  Tool = -> prism027
FEATURE [Part::Fuse] Group014
  Base = -> Group012
  Placement = pos=(30.1,10,0) rot=(0,0,1;0rad)
  Tool = -> Group013
FEATURE [Part::Feature] polygon002
  shape: bbox 28 x 8 x 2e-07 mm, 1 faces, 0 solids (baked)
FEATURE [Part::FeaturePython] RefineLinearExtrude002  # WARN: FeaturePython — macro-defined, semantics opaque (R4)
  Base = -> polygon002
FEATURE [Part::Extrusion] LinearExtrude002
  Base = -> RefineLinearExtrude002
  Dir = (0,0,42.5)
  Placement = pos=(51.35,20,22.5) rot=(-0.57735,0.57735,0.57735;4.18879rad)
  Solid = true
FEATURE [Part::Prism] prism028
  Circumradius = 11
  Height = 6
  Placement = pos=(0,3,0) rot=(1,0,0;1.5708rad)
  Polygon = 30
FEATURE [Part::Prism] prism029
  Circumradius = 8
  Height = 6
  Placement = pos=(0,3,0) rot=(1,0,0;1.5708rad)
  Polygon = 40
FEATURE [Part::Cut] difference004
  Base = -> prism028
  Placement = pos=(30.1,10,22.5) rot=(0,0,1;0rad)
  Tool = -> prism029
FEATURE [Part::Fuse] Group015
  Base = -> LinearExtrude002
  Tool = -> difference004
FEATURE [Part::MultiFuse] union005
  Shapes = -> [prism020,cube013,prism021,cube014,Group011,Group014,Group015]
FEATURE [Part::Cut] difference005
  Base = -> union004
  Tool = -> union005
FEATURE [Part::Feature] Part__Feature208  label="CustomBushingXYBlockFromSTL"
  Placement = pos=(200,-30,171) rot=(0,0,1;1.5708rad)
  shape: bbox 42.5 x 60.2 x 30.5 mm, 736 faces (baked)
FEATURE [Part::Feature] Part__Feature209  label="CustomBushingXYBlockFromSTL001"
  Placement = pos=(200,30,171) rot=(0.707107,-0.707107,0;3.14159rad)
  shape: bbox 42.5 x 60.2 x 30.5 mm, 736 faces (baked)
FEATURE [Part::Feature] Part__Feature210  label="CustomBushingXYBlockFromSTL002"
  Placement = pos=(-200,30,171) rot=(0,0,-1;1.5708rad)
  shape: bbox 42.5 x 60.2 x 30.5 mm, 736 faces (baked)
FEATURE [Part::Feature] Part__Feature211  label="CustomBushingXYBlockFromSTL003"
  Placement = pos=(-200,-30,171) rot=(0.707107,0.707107,0;3.14159rad)
  shape: bbox 42.5 x 60.2 x 30.5 mm, 736 faces (baked)
FEATURE [Part::Feature] Part__Feature217  label="BottomSupport1"
  Placement = pos=(200,200,-280) rot=(0.707107,-0.707107,0;3.14159rad)
  shape: bbox 40 x 40 x 5 mm, 21 faces (baked)
FEATURE [Part::Feature] Part__Feature218  label="BottomOuterCornerSupport2"
  Placement = pos=(200,-200,-280) rot=(0.57735,-0.57735,0.57735;2.0944rad)
  shape: bbox 40 x 5 x 40 mm, 21 faces (baked)
FEATURE [Part::Feature] Part__Feature219  label="BottomOuterCornerSupport3"
  Placement = pos=(200,-200,-280) rot=(0.57735,0.57735,0.57735;2.0944rad)
  shape: bbox 5 x 40 x 40 mm, 21 faces (baked)
FEATURE [Part::Feature] Part__Feature220  label="BottomOuterCornerSupport4"
  Placement = pos=(-200,-200,-280) rot=(1,0,0;1.5708rad)
  shape: bbox 40 x 5 x 40 mm, 21 faces (baked)
FEATURE [Part::Feature] Part__Feature221  label="BotttomOuterCornerSupport5"
  Placement = pos=(-200,200,-280) rot=(0.57735,0.57735,0.57735;4.18879rad)
  shape: bbox 40 x 5 x 40 mm, 21 faces (baked)
FEATURE [Part::Feature] Part__Feature222  label="BottomOuterCornerSupport6"
  Placement = pos=(200,200,-280) rot=(0.707107,0,0.707107;3.14159rad)
  shape: bbox 5 x 40 x 40 mm, 21 faces (baked)
FEATURE [Part::Feature] Part__Feature223  label="BottomOuterCornerSupport7"
  Placement = pos=(-200,-200,-280) rot=(0,-1,0;1.5708rad)
  shape: bbox 5 x 40 x 40 mm, 21 faces (baked)
FEATURE [Part::Feature] Part__Feature224  label="BottomOuterCornerSupport8"
  Placement = pos=(-200,200,-280) rot=(0.57735,-0.57735,-0.57735;2.0944rad)
  shape: bbox 5 x 40 x 40 mm, 21 faces (baked)
FEATURE [Part::Feature] Part__Feature225  label="BottomOuterCornerSupport9"
  Placement = pos=(200,200,-280) rot=(0,0.707107,0.707107;3.14159rad)
  shape: bbox 40 x 5 x 40 mm, 21 faces (baked)
FEATURE [Part::Feature] Part__Feature226  label="BottomSupport2"
  Placement = pos=(200,-200,-280) rot=(0,1,0;3.14159rad)
  shape: bbox 40 x 40 x 5 mm, 21 faces (baked)
FEATURE [Part::Feature] Part__Feature227  label="BottomSupport3"
  Placement = pos=(-200,200,-280) rot=(1,0,0;3.14159rad)
  shape: bbox 40 x 40 x 5 mm, 21 faces (baked)
FEATURE [Part::Feature] Part__Feature228  label="BottomSupport4"
  Placement = pos=(-200,-200,-280) rot=(0.707107,0.707107,0;3.14159rad)
  shape: bbox 40 x 40 x 5 mm, 21 faces (baked)
FEATURE [Part::Feature] Part__Feature241  label="Alu-20x20x404"
  Placement = pos=(0,0,10) rot=(0,0,1;0rad)
  shape: bbox 360 x 20 x 20 mm, 40 faces (baked)
FEATURE [Part::Feature] Part__Feature159  label="motor-block-top-mirrored"
  shape: bbox 105 x 62 x 12 mm, 56 faces (baked)
FEATURE [Part::Feature] Part__Feature246  label="XYBlock1_Bushing1"
  Placement = pos=(-190,-2,171) rot=(1,0,0;1.5708rad)
  shape: bbox 12.99 x 30 x 12.99 mm, 6 faces (baked)
FEATURE [Part::Feature] Part__Feature247  label="XYBlock1_Bushing2"
  Placement = pos=(-190,33,171) rot=(1,0,0;1.5708rad)
  shape: bbox 12.99 x 30 x 12.99 mm, 6 faces (baked)
FEATURE [Part::Feature] Part__Feature248  label="XYBlock2_Bushing1"
  Placement = pos=(190,-3,171) rot=(1,0,0;1.5708rad)
  shape: bbox 12.99 x 30 x 12.99 mm, 6 faces (baked)
FEATURE [Part::Feature] Part__Feature249  label="XYBlock2_Bushing2"
  Placement = pos=(190,33,171) rot=(1,0,0;1.5708rad)
  shape: bbox 12.99 x 30 x 12.99 mm, 6 faces (baked)
FEATURE [Part::Feature] Part__Feature250  label="Fillet"
  Placement = pos=(0,0,193.5) rot=(0,1,0;1.5708rad)
  shape: bbox 30 x 12.99 x 12.99 mm, 6 faces (baked)
FEATURE [Part::Feature] Part__Feature251  label="Fillet001"
  Placement = pos=(0,0,148.5) rot=(0,1,0;1.5708rad)
  shape: bbox 30 x 12.99 x 12.99 mm, 6 faces (baked)
FEATURE [Part::Feature] Part__Feature252  label="Fillet002"
  Placement = pos=(-32,1,148.5) rot=(0,1,0;1.5708rad)
  shape: bbox 30 x 12.99 x 12.99 mm, 6 faces (baked)
FEATURE [Part::Feature] Part__Feature253  label="Fillet003"
  Placement = pos=(-32,0,193.5) rot=(0,1,0;1.5708rad)
  shape: bbox 30 x 12.99 x 12.99 mm, 6 faces (baked)
FEATURE [Part::Feature] Part__Feature254  label="Pocket"
  Placement = pos=(200,-200,220) rot=(0,1,0;1.5708rad)
  shape: bbox 5 x 40 x 40 mm, 21 faces (baked)
FEATURE [Part::Feature] Part__Feature255  label="Pocket001"
  Placement = pos=(200,200,220) rot=(-0.573962,0.584068,0.573962;2.08435rad)
  shape: bbox 40.05 x 5.662 x 40 mm, 21 faces (baked)
FEATURE [Part::Feature] Part__Feature256  label="Pocket002"
  Placement = pos=(200,200,220) rot=(-0.573962,0.584068,-0.573962;2.08435rad)
  shape: bbox 5 x 40.69 x 40.34 mm, 21 faces (baked)
FEATURE [Part::Feature] Part__Feature257  label="Pocket003"
  Placement = pos=(200,-200,220) rot=(0,-0.707107,0.707107;3.14159rad)
  shape: bbox 40 x 5 x 40 mm, 21 faces (baked)
FEATURE [Part::Feature] Part__Feature258  label="Pocket004"
  Placement = pos=(-200,-200,220) rot=(-0.57735,-0.57735,0.57735;2.0944rad)
  shape: bbox 5 x 40 x 40 mm, 21 faces (baked)
FEATURE [Part::Feature] Part__Feature259  label="Pocket005"
  Placement = pos=(-200,200,220) rot=(-0.707093,0.006171,0.707093;3.12925rad)
  shape: bbox 5.662 x 40.05 x 40 mm, 21 faces (baked)
FEATURE [Part::Feature] Part__Feature260  label="Pocket006"
  Placement = pos=(-200,-200,220) rot=(-0.58068,-0.570633,0.58068;4.17868rad)
  shape: bbox 40.05 x 5.662 x 40 mm, 21 faces (baked)
FEATURE [Part::Feature] Part__Feature261  label="Pocket007"
  Placement = pos=(-200,200,220) rot=(-1,0,0;1.5708rad)
  shape: bbox 40 x 5 x 40 mm, 21 faces (baked)
FEATURE [Part::Feature] Part__Feature263  label="LeftMotorBlockSpacer"
  Placement = pos=(-215.5,173.5,190) rot=(0,0,1;0rad)
  shape: bbox 105 x 62 x 30 mm, 28 faces (baked)
FEATURE [Part::Feature] Part__Feature264  label="RightMotorBlockSpacer"
  Placement = pos=(180,160,190) rot=(0,0,1;0rad)
  shape: bbox 105 x 62 x 30 mm, 28 faces (baked)
FEATURE [Part::Feature] Part__Feature265  label="LeftIdlerBlockSpacer"
  Placement = pos=(-111.3,-181.45,190) rot=(0,0,1;3.14159rad)
  shape: bbox 60 x 40 x 30 mm, 25 faces (baked)
FEATURE [Part::Feature] Part__Feature266  label="RightIdlerBlockSpacer"
  Placement = pos=(200,-160,190) rot=(0,0,1;3.14159rad)
  shape: bbox 60 x 40 x 30 mm, 25 faces (baked)
FEATURE [Part::Feature] Part__Feature267  label="Pocket008"
  Placement = pos=(-200,-200,220) rot=(0,0,1;0rad)
  shape: bbox 40 x 40 x 5 mm, 21 faces (baked)
FEATURE [Part::Feature] Part__Feature268  label="Pocket009"
  Placement = pos=(200,-200,220) rot=(0,0,1;1.5708rad)
  shape: bbox 40 x 40 x 5 mm, 21 faces (baked)
FEATURE [Part::Feature] Part__Feature269  label="Pocket010"
  Placement = pos=(200,200,220) rot=(0,0,1;3.14159rad)
  shape: bbox 40 x 40 x 5 mm, 21 faces (baked)
FEATURE [Part::Feature] Part__Feature270  label="Pocket011"
  Placement = pos=(-200,200,220) rot=(0,0,-1;1.5708rad)
  shape: bbox 40 x 40 x 5 mm, 21 faces (baked)
FEATURE [Part::Feature] Part__Feature271  label="InnerCornerBracket"
  Placement = pos=(-180,180,-260) rot=(0,0,1;1.5708rad)
  shape: bbox 40 x 40 x 43 mm, 48 faces (baked)
FEATURE [Part::Feature] Part__Feature272  label="InnerCornerBracket001"
  Placement = pos=(180,180,-260) rot=(0,0,1;0rad)
  shape: bbox 40 x 40 x 43 mm, 48 faces (baked)
FEATURE [Part::Feature] Part__Feature273  label="InnerCornerBracket002"
  Placement = pos=(180,-180,-260) rot=(0,0,-1;1.5708rad)
  shape: bbox 40 x 40 x 43 mm, 48 faces (baked)
FEATURE [Part::Feature] Part__Feature274  label="InnerCornerBracket003"
  Placement = pos=(-180,-180,-260) rot=(0,0,1;3.14159rad)
  shape: bbox 40 x 40 x 43 mm, 48 faces (baked)
FEATURE [Part::Feature] Part__Feature275  label="XCarriage_Bushingmod_Step_AP214"
  Placement = pos=(0,-15,171) rot=(0,0,1;0rad)
  shape: bbox 68 x 16 x 75.18 mm, 261 faces (baked)
FEATURE [Part::Feature] Part__Feature276  label="Chimera-Mount"
  Placement = pos=(-15,-40,155) rot=(0,0,1;0rad)
  shape: bbox 50 x 23 x 25 mm, 21 faces (baked)
FEATURE [Part::Feature] Part__Feature277  label="Alu-20x20x401"
  Placement = pos=(0,0,-100) rot=(0,0,1;0rad)
  shape: bbox 20 x 20 x 500 mm, 39 faces (baked)
FEATURE [Part::Feature] Part__Feature278  label="Alu-20x20x405"
  Placement = pos=(380,0,-100) rot=(0,0,1;0rad)
  shape: bbox 20 x 20 x 500 mm, 39 faces (baked)
FEATURE [Part::Feature] Part__Feature279  label="Alu-20x20x406"
  Placement = pos=(0,380,-100) rot=(0,0,1;0rad)
  shape: bbox 20 x 20 x 500 mm, 39 faces (baked)
FEATURE [Part::Feature] Part__Feature280  label="Alu-20x20x407"
  Placement = pos=(380,380,-100) rot=(0,0,1;0rad)
  shape: bbox 20 x 20 x 500 mm, 39 faces (baked)
FEATURE [Part::Feature] Part__Feature281  label="Z-Axis-Rod-500mm"
  Placement = pos=(70,158,-280) rot=(0,0,1;0rad)
  shape: bbox 12 x 12 x 500 mm, 3 faces (baked)
FEATURE [Part::Feature] Part__Feature282  label="Z-Axis-Rod-500mm001"
  Placement = pos=(-70,158,-280) rot=(0,0,1;0rad)
  shape: bbox 12 x 12 x 500 mm, 3 faces (baked)
FEATURE [Part::Feature] Part__Feature283  label="Coupler_5mm_to_8mm"
  Placement = pos=(0,160,165) rot=(1,0,0;3.14159rad)
  shape: bbox 26.62 x 26.44 x 24.5 mm, 22 faces (baked)
FEATURE [Part::Feature] Part__Feature284  label="LM12LUU_1"
  Placement = pos=(-70,160,-230) rot=(0,0,1;0rad)
  shape: bbox 22.73 x 22.73 x 57 mm, 6 faces (baked)
FEATURE [Part::Feature] Part__Feature285  label="LM12LUU_2"
  Placement = pos=(70,158,-230) rot=(0,0,1;0rad)
  shape: bbox 22.73 x 22.73 x 57 mm, 6 faces (baked)
